# Revit family: Sink-Single Bowl-Clark Prism Large Under Over Mount1
name_source: partatom
category: Plumbing Fixtures
revit_build: Autodesk Revit 2014 (Build: 20140709_2115(x64)
units: mm (PartAtom-declared; Revit-internal decimal feet)

## types (1)
- Prism
    Assembly Code = D2010410
    CW Connection = No
    Capacity_ANZRS = 0.0 L
    Cost = 0 $
    Default Elevation = 0 mm  [stored 0 ft]
    Depth_ANZRS = 200 mm  [stored 0.656168 ft]
    Description = The Clark Prism sink range gives you the flexibility of installing undermount or overmount. It consists of Single Bowl, 1.5 Bowl and Double Bowl Undermount. Select a single bowl if you’re short on space or go for a pair for added practicality.
    HW Connection = No
    Keynote = SK
    Length_ANZRS = 760 mm
    Manufacturer = GWA Bathrooms & Kitchens
    Material_ANZRS = Metal-Stainless-Caroma
    Model = PPR10LGB
    ModifiedIssue_ANZRS = 20150616 $
    Type Comments = Clark Prism Single Large Bowl Undermount/Overmount Sink
    URL = http://specify.caroma.com.au
    Vent Connection = No
    WFU = 2
    Waste Connection = Yes
    Waste Radius = 25 mm  [stored 0.082021 ft]
    Width_ANZRS = 440 mm  [stored 1.44357 ft]

note: [stored X ft] marks values corroborated as IEEE doubles in the binary element streams (Revit-internal decimal feet)

## geometry (parser evidence)
native form markers: Blend x14, Sweep x3
no freeform markers — native parametric forms only
